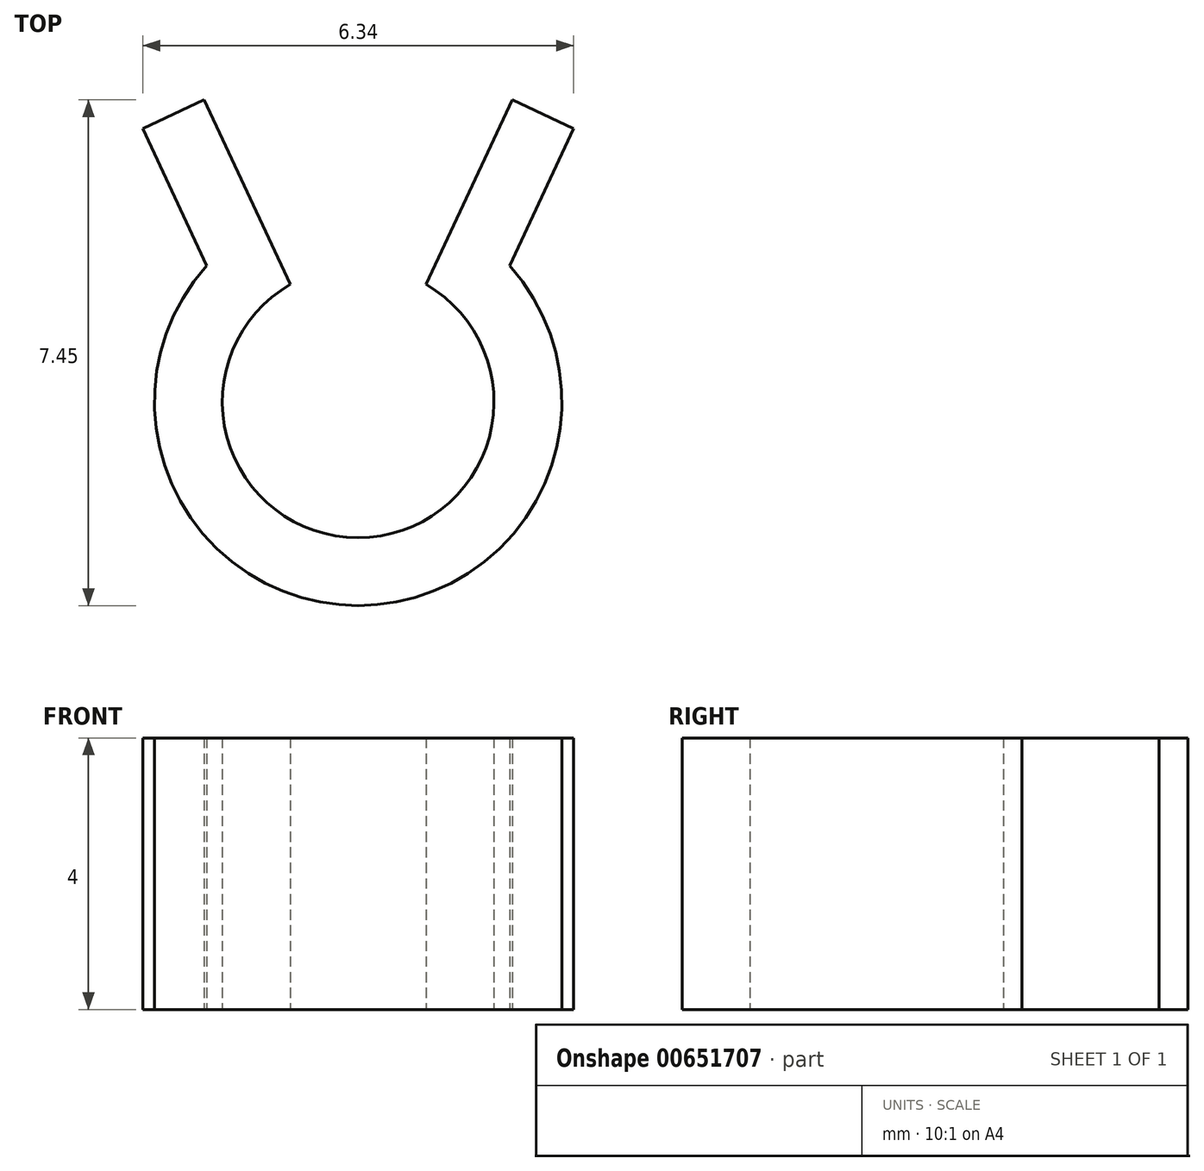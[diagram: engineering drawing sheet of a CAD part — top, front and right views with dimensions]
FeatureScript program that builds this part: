
annotation { "Feature Type Name" : "Feature", "Feature Type Description" : "" }
export const myFeature = defineFeature(function(context is Context, id is Id, definition is map)
    precondition{}
    {
        {
            var Q0;
            Q0=qCreatedBy(makeId("Top.planeOp"),FACE);
            var sketch = newSketch(context, id + "F0", { "sketchPlane" : qUnion([Q0])});
            skCircle(sketch, "E0", {"center": v(0, 0) * mm, "radius": 2 * mm});
            skArc(sketch, "E1.0", {"start": v(-2.23, 2) * mm, "mid": v(0, -3) * mm, "end": v(2.23, 2) * mm});
            skLineSegment(sketch, "E2", {"start": v(0, 0) * mm, "end": v(0, 3) * mm, "construction": true});
            skLineSegment(sketch, "E3", {"start": v(-1.42, 2.64) * mm, "end": v(-1, 1.73) * mm, "construction": true});
            skLineSegment(sketch, "E4", {"start": v(-1, 1.73) * mm, "end": v(-2.27, 4.45) * mm});
            skLineSegment(sketch, "E5", {"start": v(-2.27, 4.45) * mm, "end": v(-3.17, 4.03) * mm});
            skLineSegment(sketch, "E6", {"start": v(-3.17, 4.03) * mm, "end": v(-2.23, 2) * mm});
            skLineSegment(sketch, "E7.MirrorCS", {"start": v(1, 1.73) * mm, "end": v(2.27, 4.45) * mm});
            skLineSegment(sketch, "E8.MirrorCS", {"start": v(2.27, 4.45) * mm, "end": v(3.17, 4.03) * mm});
            skLineSegment(sketch, "E9.MirrorCS", {"start": v(3.17, 4.03) * mm, "end": v(2.23, 2) * mm});
            skArc(sketch, "E10.trimOffspring", {"start": v(1.42, 2.64) * mm, "mid": v(0, 3) * mm, "end": v(-1.42, 2.64) * mm, "construction": true});
            skSolve(sketch);
        }
        {
            var Q0;
            Q0=makeQuery(id+"F0.imprint","IMPRINT",FACE,{"disambiguationData":[TD([[makeQuery(id+"F0.imprint","IMPRINT",EDGE,{"derivedFrom":sQuery(id+"F0.wireOp",EDGE,"E1.0")}),1.0]])]});
            extrude(context, id + "F1", {"entities" : qUnion([Q0]), "depth" : 4 * mm, "offsetDistance" : 25 * mm});
        }
    });
